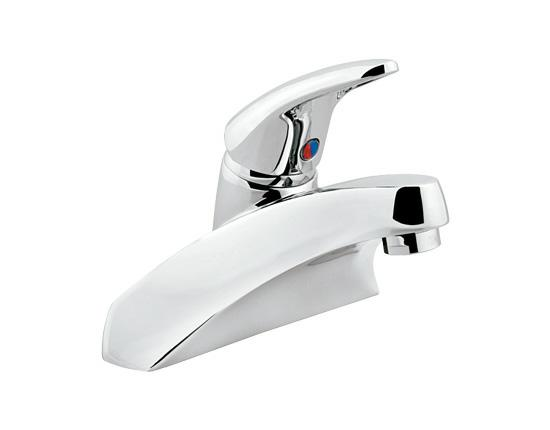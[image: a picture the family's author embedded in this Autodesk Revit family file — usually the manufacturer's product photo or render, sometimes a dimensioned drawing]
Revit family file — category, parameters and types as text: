
# Revit family: Mezcladora 4 EP-92
name_source: partatom
category: Plumbing Fixtures
revit_build: Autodesk Revit 2015 (Build: 20140223_1515(x64)
units: mm (PartAtom-declared; Revit-internal decimal feet)

## types (1)
- EP-92
    Brass Chromed = Brass
    Default Elevation = 1"
    Description = Mezcladora de 4” con desagüe de push y rebosadero
Mezcladora de 4" con Desagüe de Push
    Features = Monomando de 4" con desagüe de push
instalación de 4" con Valvex V izq. y der. de
discos cerámicos de 1/4 de vuelta.
Mecladora para lavabo con desagüe de push, instalación de 4" con Valvex V izq. y der. de discos cerámicos de 1/4 de vuelta.
    Inlet Threads = ½" - 14 NPSM
    Manufacturer = HELVEX S.A. de C.V.
    Max. Working Pressure = 85.3 psi
    Min. Working Pressure = 2.8 psi
    Model = EP-92
    Satin = Satín Duravex
    Total Height = 5"
    Total Length = 6"
    Total Width = 4"
    Type Comments = Monomando de 4”
    Type Image = EP-92.jpg
    URL = http://www.helvex.com.mx

## geometry (parser evidence)
native form markers: Sweep x3
no freeform markers — native parametric forms only
